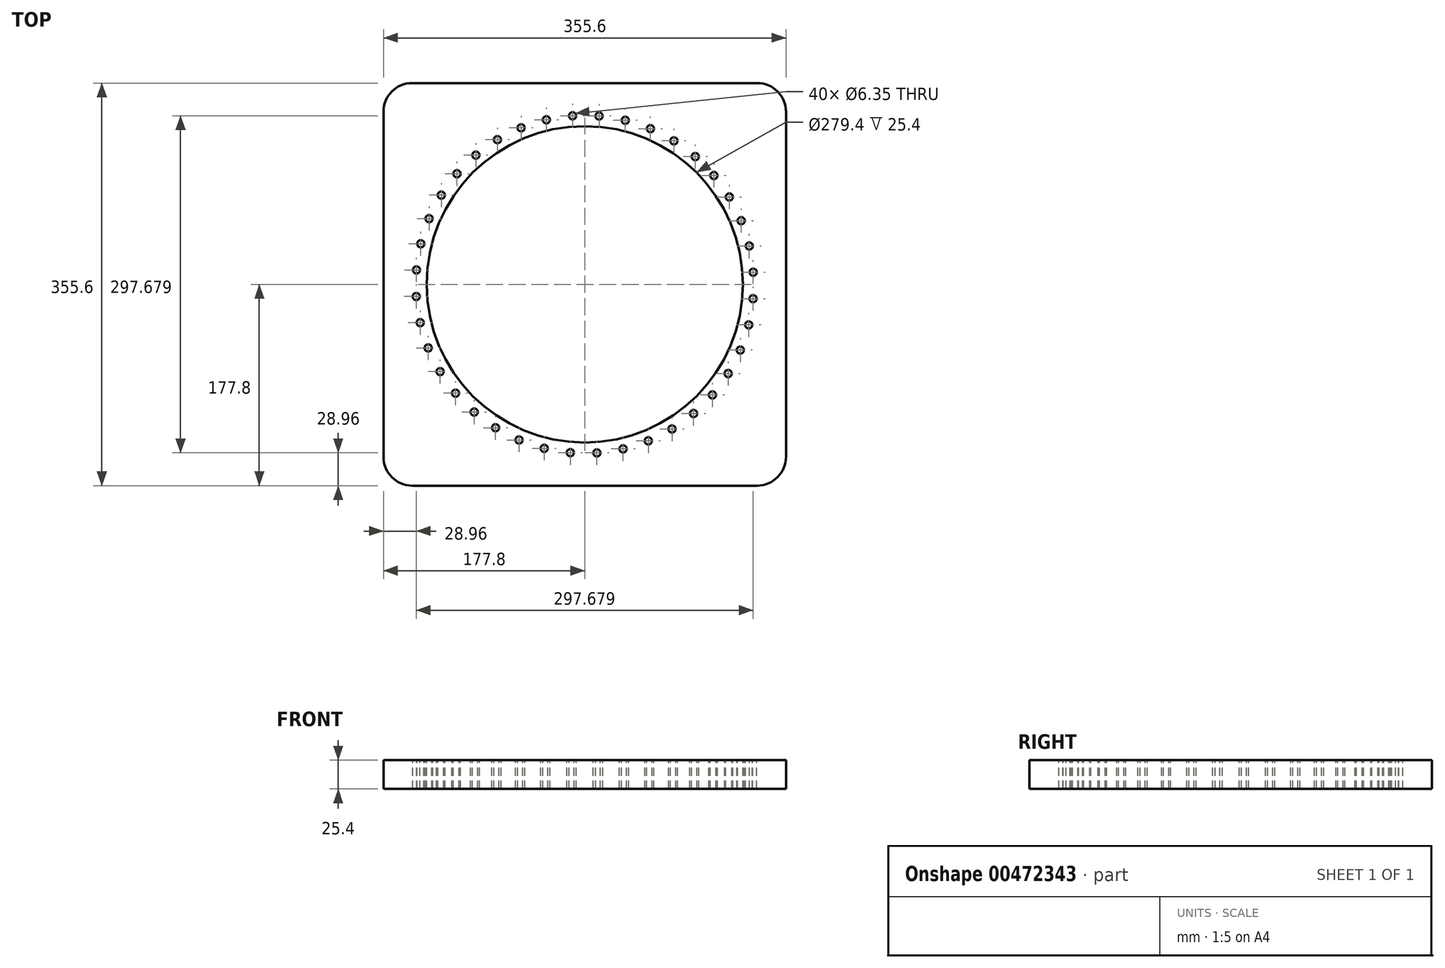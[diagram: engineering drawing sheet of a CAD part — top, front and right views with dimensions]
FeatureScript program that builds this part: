
annotation { "Feature Type Name" : "Feature", "Feature Type Description" : "" }
export const myFeature = defineFeature(function(context is Context, id is Id, definition is map)
    precondition{}
    {
        {
            var Q0;
            Q0=qCreatedBy(makeId("Top.planeOp"),FACE);
            var sketch = newSketch(context, id + "F0", { "sketchPlane" : qUnion([Q0])});
            skLineSegment(sketch, "E0.bottom", {"start": v(152.4, -177.8) * mm, "end": v(-152.4, -177.8) * mm});
            skLineSegment(sketch, "E0.top", {"start": v(152.4, 177.8) * mm, "end": v(-152.4, 177.8) * mm});
            skLineSegment(sketch, "E0.left", {"start": v(177.8, -152.4) * mm, "end": v(177.8, 152.4) * mm});
            skLineSegment(sketch, "E0.right", {"start": v(-177.8, -152.4) * mm, "end": v(-177.8, 152.4) * mm});
            skPoint(sketch, "E0.middle", {"position": v(0, 0) * mm});
            skPoint(sketch, "E1.visualSharp", {"position": v(-177.8, 177.8) * mm});
            skArc(sketch, "E1.filletArc", {"start": v(-152.4, 177.8) * mm, "mid": v(-170.36, 170.36) * mm, "end": v(-177.8, 152.4) * mm});
            skPoint(sketch, "E2.visualSharp", {"position": v(177.8, 177.8) * mm});
            skArc(sketch, "E2.filletArc", {"start": v(177.8, 152.4) * mm, "mid": v(170.36, 170.36) * mm, "end": v(152.4, 177.8) * mm});
            skPoint(sketch, "E3.visualSharp", {"position": v(177.8, -177.8) * mm});
            skArc(sketch, "E3.filletArc", {"start": v(152.4, -177.8) * mm, "mid": v(170.36, -170.36) * mm, "end": v(177.8, -152.4) * mm});
            skPoint(sketch, "E4.visualSharp", {"position": v(-177.8, -177.8) * mm});
            skArc(sketch, "E4.filletArc", {"start": v(-177.8, -152.4) * mm, "mid": v(-170.36, -170.36) * mm, "end": v(-152.4, -177.8) * mm});
            skSolve(sketch);
        }
        {
            var Q0;
            Q0 = qSketchRegion(id + "F0", true);
            extrude(context, id + "F1", {"entities" : qUnion([Q0]), "depth" : 25.4 * mm});
        }
        {
            var Q0;
            Q0=makeQuery(id+"F1.opExtrude","CAP_FACE",FACE,{"disambiguationData":[OSD([sQuery(id+"F0.wireOp",EDGE,"E0.bottom"),sQuery(id+"F0.wireOp",EDGE,"E0.top"),sQuery(id+"F0.wireOp",EDGE,"E0.left"),sQuery(id+"F0.wireOp",EDGE,"E0.right"),sQuery(id+"F0.wireOp",EDGE,"E1.filletArc"),sQuery(id+"F0.wireOp",EDGE,"E2.filletArc"),sQuery(id+"F0.wireOp",EDGE,"E3.filletArc"),sQuery(id+"F0.wireOp",EDGE,"E4.filletArc")])],"isStart":false});
            var sketch = newSketch(context, id + "F2", { "sketchPlane" : qUnion([Q0])});
            skCircle(sketch, "E5", {"center": v(0, 0) * mm, "radius": 139.7 * mm});
            skSolve(sketch);
        }
        {
            var Q0;
            Q0 = qSketchRegion(id + "F2", true);
            extrude(context, id + "F3", {"entities" : qUnion([Q0]), "operationType" : NewBodyOperationType.REMOVE, "oppositeDirection" : true, "depth" : 25.4 * mm});
        }
        {
            var Q0;
            Q0=makeQuery(id+"F1.opExtrude","CAP_FACE",FACE,{"disambiguationData":[OSD([sQuery(id+"F0.wireOp",EDGE,"E0.bottom"),sQuery(id+"F0.wireOp",EDGE,"E0.top"),sQuery(id+"F0.wireOp",EDGE,"E0.left"),sQuery(id+"F0.wireOp",EDGE,"E0.right"),sQuery(id+"F0.wireOp",EDGE,"E1.filletArc"),sQuery(id+"F0.wireOp",EDGE,"E2.filletArc"),sQuery(id+"F0.wireOp",EDGE,"E3.filletArc"),sQuery(id+"F0.wireOp",EDGE,"E4.filletArc")])],"isStart":false});
            var sketch = newSketch(context, id + "F4", { "sketchPlane" : qUnion([Q0])});
            skCircle(sketch, "E6", {"center": v(-148.68, 12.7) * mm, "radius": 3.18 * mm});
            skCircle(sketch, "E7.1.0", {"center": v(-148.84, -10.72) * mm, "radius": 3.18 * mm});
            skCircle(sketch, "E7.2.0", {"center": v(-145.33, -33.87) * mm, "radius": 3.18 * mm});
            skCircle(sketch, "E7.3.0", {"center": v(-138.24, -56.19) * mm, "radius": 3.18 * mm});
            skCircle(sketch, "E7.4.0", {"center": v(-127.75, -77.12) * mm, "radius": 3.18 * mm});
            skCircle(sketch, "E7.5.0", {"center": v(-114.12, -96.16) * mm, "radius": 3.18 * mm});
            skCircle(sketch, "E7.6.0", {"center": v(-97.67, -112.82) * mm, "radius": 3.18 * mm});
            skCircle(sketch, "E7.7.0", {"center": v(-78.82, -126.71) * mm, "radius": 3.18 * mm});
            skCircle(sketch, "E7.8.0", {"center": v(-58.02, -137.48) * mm, "radius": 3.18 * mm});
            skCircle(sketch, "E7.9.0", {"center": v(-35.8, -144.87) * mm, "radius": 3.18 * mm});
            skCircle(sketch, "E7.10.0", {"center": v(-12.7, -148.68) * mm, "radius": 3.18 * mm});
            skCircle(sketch, "E7.11.0", {"center": v(10.72, -148.84) * mm, "radius": 3.18 * mm});
            skCircle(sketch, "E7.12.0", {"center": v(33.87, -145.33) * mm, "radius": 3.18 * mm});
            skCircle(sketch, "E7.13.0", {"center": v(56.19, -138.24) * mm, "radius": 3.18 * mm});
            skCircle(sketch, "E7.14.0", {"center": v(77.12, -127.75) * mm, "radius": 3.17 * mm});
            skCircle(sketch, "E7.15.0", {"center": v(96.16, -114.12) * mm, "radius": 3.18 * mm});
            skCircle(sketch, "E7.16.0", {"center": v(112.82, -97.67) * mm, "radius": 3.18 * mm});
            skCircle(sketch, "E7.17.0", {"center": v(126.71, -78.82) * mm, "radius": 3.18 * mm});
            skCircle(sketch, "E7.18.0", {"center": v(137.48, -58.02) * mm, "radius": 3.18 * mm});
            skCircle(sketch, "E7.19.0", {"center": v(144.87, -35.8) * mm, "radius": 3.18 * mm});
            skCircle(sketch, "E7.20.0", {"center": v(148.68, -12.7) * mm, "radius": 3.18 * mm});
            skCircle(sketch, "E7.21.0", {"center": v(148.84, 10.72) * mm, "radius": 3.18 * mm});
            skCircle(sketch, "E7.22.0", {"center": v(145.33, 33.87) * mm, "radius": 3.18 * mm});
            skCircle(sketch, "E7.23.0", {"center": v(138.24, 56.19) * mm, "radius": 3.18 * mm});
            skCircle(sketch, "E7.24.0", {"center": v(127.75, 77.12) * mm, "radius": 3.18 * mm});
            skCircle(sketch, "E7.25.0", {"center": v(114.12, 96.16) * mm, "radius": 3.18 * mm});
            skCircle(sketch, "E7.26.0", {"center": v(97.67, 112.82) * mm, "radius": 3.18 * mm});
            skCircle(sketch, "E7.27.0", {"center": v(78.82, 126.71) * mm, "radius": 3.18 * mm});
            skCircle(sketch, "E7.28.0", {"center": v(58.02, 137.48) * mm, "radius": 3.18 * mm});
            skCircle(sketch, "E7.29.0", {"center": v(35.8, 144.87) * mm, "radius": 3.17 * mm});
            skCircle(sketch, "E7.30.0", {"center": v(12.7, 148.68) * mm, "radius": 3.18 * mm});
            skCircle(sketch, "E7.31.0", {"center": v(-10.72, 148.84) * mm, "radius": 3.18 * mm});
            skCircle(sketch, "E7.32.0", {"center": v(-33.87, 145.33) * mm, "radius": 3.18 * mm});
            skCircle(sketch, "E7.33.0", {"center": v(-56.19, 138.24) * mm, "radius": 3.18 * mm});
            skCircle(sketch, "E7.34.0", {"center": v(-77.12, 127.75) * mm, "radius": 3.18 * mm});
            skCircle(sketch, "E7.35.0", {"center": v(-96.16, 114.12) * mm, "radius": 3.18 * mm});
            skCircle(sketch, "E7.36.0", {"center": v(-112.82, 97.67) * mm, "radius": 3.18 * mm});
            skCircle(sketch, "E7.37.0", {"center": v(-126.71, 78.82) * mm, "radius": 3.18 * mm});
            skCircle(sketch, "E7.38.0", {"center": v(-137.48, 58.02) * mm, "radius": 3.18 * mm});
            skCircle(sketch, "E7.39.0", {"center": v(-144.87, 35.8) * mm, "radius": 3.18 * mm});
            skPoint(sketch, "E7.center", {"position": v(0, 0) * mm});
            skSolve(sketch);
        }
        {
            var Q0;
            Q0 = qSketchRegion(id + "F4", true);
            extrude(context, id + "F5", {"entities" : qUnion([Q0]), "operationType" : NewBodyOperationType.REMOVE, "endBound" : BoundingType.THROUGH_ALL, "oppositeDirection" : true, "depth" : 25.4 * mm});
        }
    });
